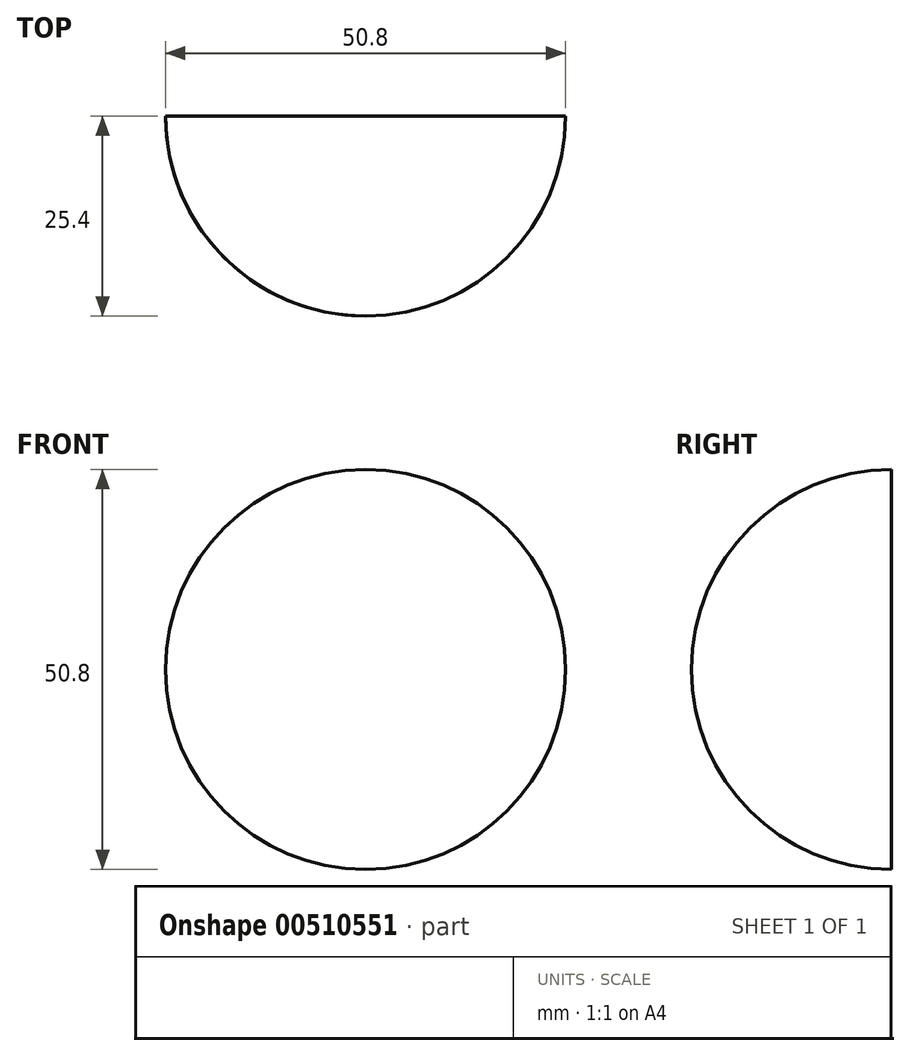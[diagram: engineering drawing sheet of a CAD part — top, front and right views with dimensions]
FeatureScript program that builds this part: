
annotation { "Feature Type Name" : "Feature", "Feature Type Description" : "" }
export const myFeature = defineFeature(function(context is Context, id is Id, definition is map)
    precondition{}
    {
        {
            var Q0;
            Q0=qCreatedBy(makeId("Top.planeOp"),FACE);
            var sketch = newSketch(context, id + "F0", { "sketchPlane" : qUnion([Q0])});
            skArc(sketch, "E0", {"start": v(0, 0) * mm, "mid": v(17.96, 7.44) * mm, "end": v(25.4, 25.4) * mm});
            skLineSegment(sketch, "E1", {"start": v(0, 25.4) * mm, "end": v(25.4, 25.4) * mm});
            skLineSegment(sketch, "E2", {"start": v(0, 25.4) * mm, "end": v(0, 0) * mm});
            skSolve(sketch);
        }
        {
            var Q0;
            Q0=makeQuery(id+"F0.imprint","IMPRINT",FACE,{"disambiguationData":[TD([[makeQuery(id+"F0.imprint","IMPRINT",EDGE,{"derivedFrom":sQuery(id+"F0.wireOp",EDGE,"E0")}),1.0]])]});
            var Q1;
            Q1=sQuery(id+"F0.wireOp",EDGE,"E2");
            revolve(context, id + "F1", {"entities" : qUnion([Q0]), "axis" : qUnion([Q1]), "revolveType" : RevolveType.FULL});
        }
    });
